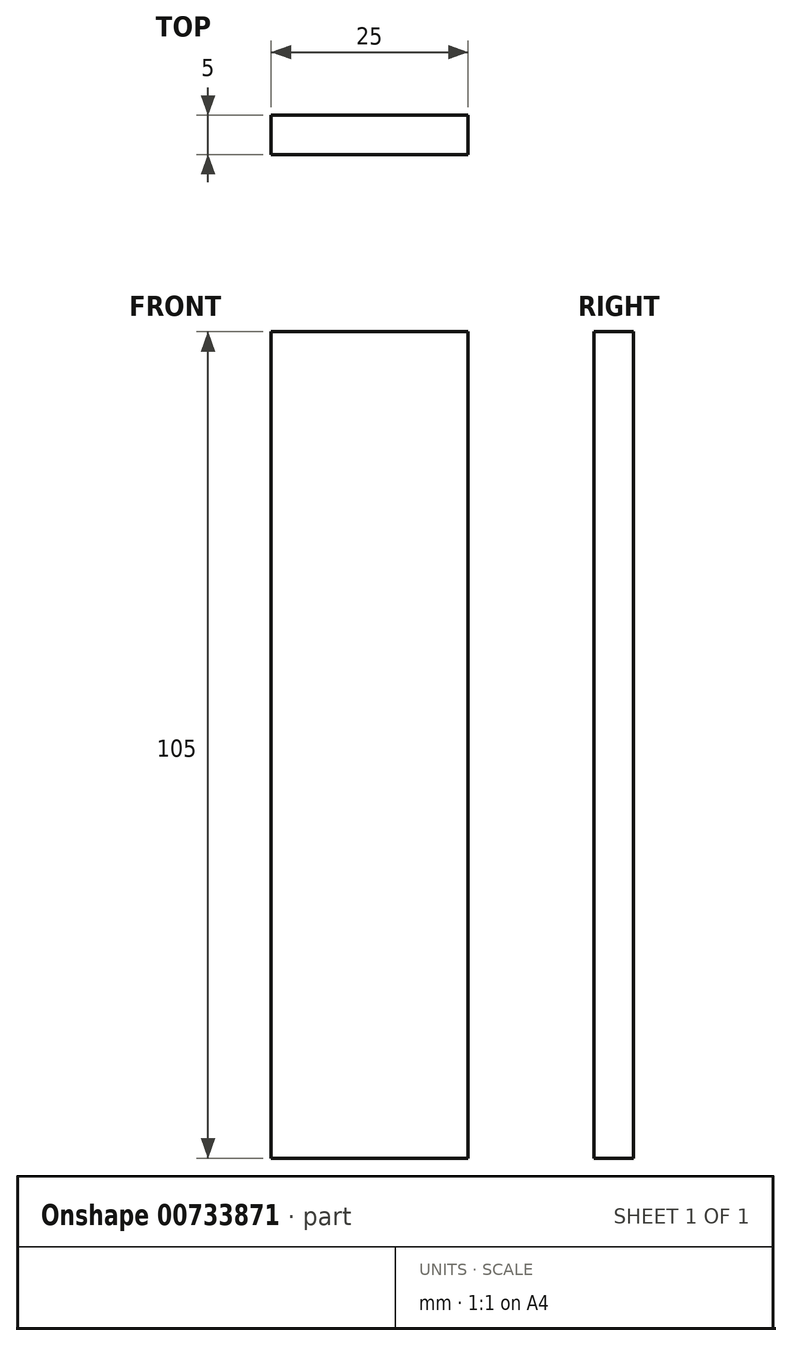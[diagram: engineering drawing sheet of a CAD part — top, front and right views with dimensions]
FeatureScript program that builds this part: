
annotation { "Feature Type Name" : "Feature", "Feature Type Description" : "" }
export const myFeature = defineFeature(function(context is Context, id is Id, definition is map)
    precondition{}
    {
        {
            var Q0;
            Q0=qCreatedBy(makeId("Front.planeOp"),FACE);
            var sketch = newSketch(context, id + "F0", { "sketchPlane" : qUnion([Q0])});
            skLineSegment(sketch, "E0.bottom", {"start": v(12.5, 52.5) * mm, "end": v(-12.5, 52.5) * mm});
            skLineSegment(sketch, "E0.top", {"start": v(12.5, -52.5) * mm, "end": v(-12.5, -52.5) * mm});
            skLineSegment(sketch, "E0.left", {"start": v(12.5, 52.5) * mm, "end": v(12.5, -52.5) * mm});
            skLineSegment(sketch, "E0.right", {"start": v(-12.5, 52.5) * mm, "end": v(-12.5, -52.5) * mm});
            skPoint(sketch, "E0.middle", {"position": v(0, 0) * mm});
            skSolve(sketch);
        }
        {
            var Q0;
            Q0=makeQuery(id+"F0.imprint","IMPRINT",FACE,{"disambiguationData":[TD([[makeQuery(id+"F0.imprint","IMPRINT",EDGE,{"derivedFrom":sQuery(id+"F0.wireOp",EDGE,"E0.bottom")}),1.0]])]});
            extrude(context, id + "F1", {"entities" : qUnion([Q0]), "depth" : 5 * mm, "offsetDistance" : 25 * mm});
        }
    });
